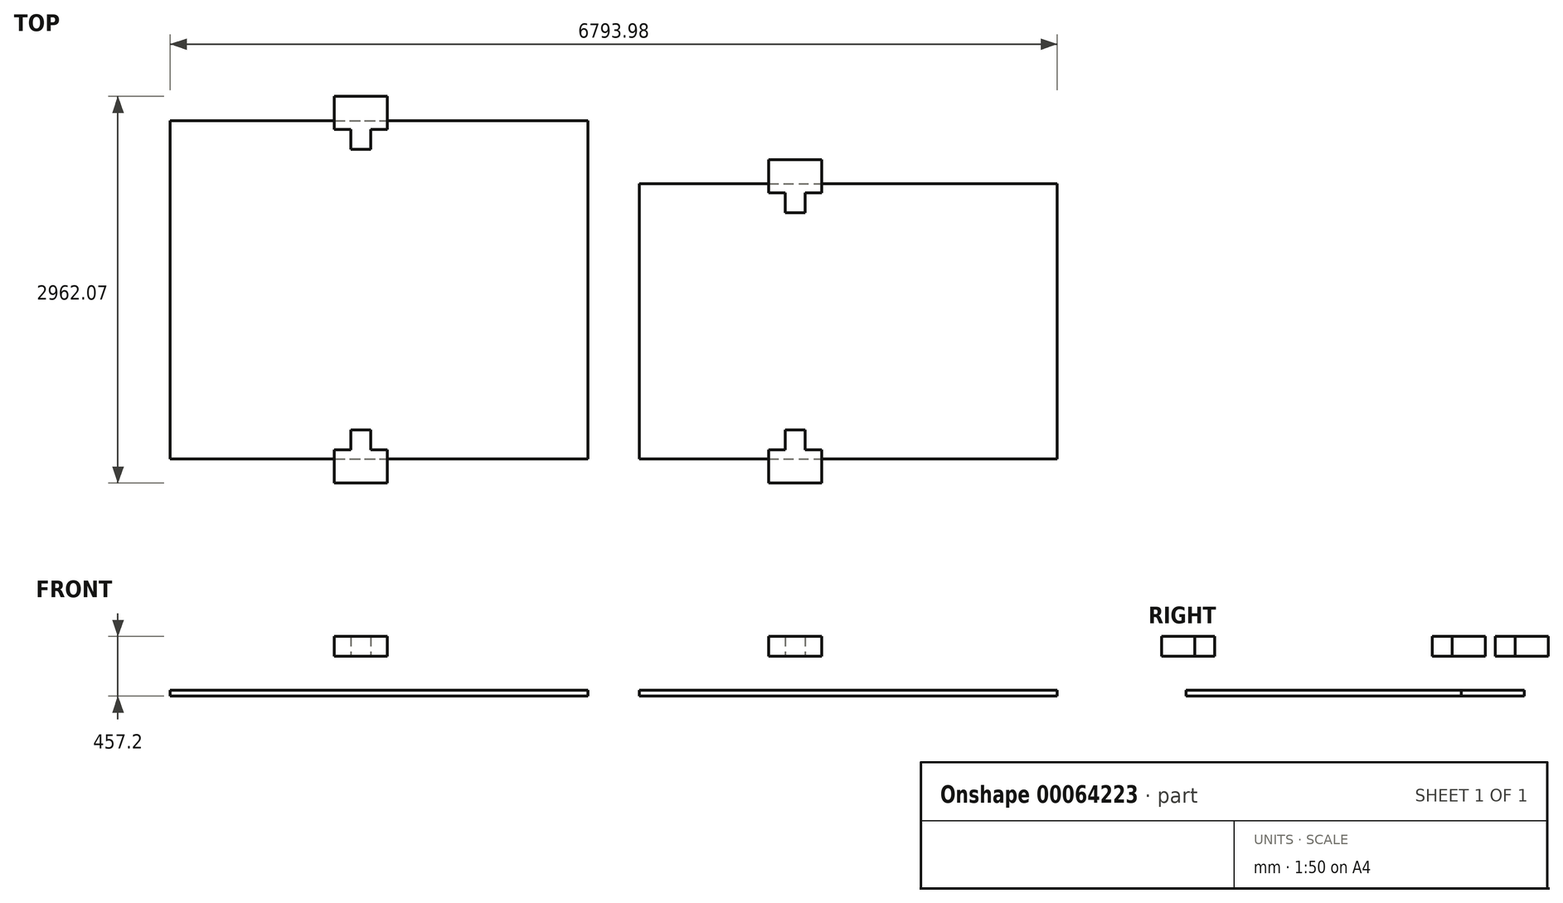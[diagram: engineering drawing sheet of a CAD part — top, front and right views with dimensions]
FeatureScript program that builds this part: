
annotation { "Feature Type Name" : "Feature", "Feature Type Description" : "" }
export const myFeature = defineFeature(function(context is Context, id is Id, definition is map)
    precondition{}
    {
        {
            var Q0;
            Q0=qCreatedBy(makeId("Top.planeOp"),FACE);
            var sketch = newSketch(context, id + "F0", { "sketchPlane" : qUnion([Q0])});
            skLineSegment(sketch, "E0.bottom", {"start": v(-1939.52, -1293.43) * mm, "end": v(1260.88, -1293.43) * mm});
            skLineSegment(sketch, "E0.top", {"start": v(-1939.52, 1297.37) * mm, "end": v(1260.88, 1297.37) * mm});
            skLineSegment(sketch, "E0.left", {"start": v(-1939.52, -1293.43) * mm, "end": v(-1939.52, 1297.37) * mm});
            skLineSegment(sketch, "E0.right", {"start": v(1260.88, -1293.43) * mm, "end": v(1260.88, 1297.37) * mm});
            skSolve(sketch);
        }
        {
            var Q0;
            Q0=makeQuery(id+"F0.imprint","IMPRINT",FACE,{"disambiguationData":[TD([[makeQuery(id+"F0.imprint","IMPRINT",EDGE,{"derivedFrom":sQuery(id+"F0.wireOp",EDGE,"E0.bottom")}),1.0]])]});
            extrude(context, id + "F1", {"entities" : qUnion([Q0]), "depth" : 44.45 * mm});
        }
        {
            var Q0;
            Q0=qCreatedBy(makeId("Top.planeOp"),FACE);
            var sketch = newSketch(context, id + "F2", { "sketchPlane" : qUnion([Q0])});
            skLineSegment(sketch, "E1.bottom", {"start": v(1654.06, 814.34) * mm, "end": v(4854.46, 814.34) * mm});
            skLineSegment(sketch, "E1.top", {"start": v(1654.06, -1293.86) * mm, "end": v(4854.46, -1293.86) * mm});
            skLineSegment(sketch, "E1.left", {"start": v(1654.06, 814.34) * mm, "end": v(1654.06, -1293.86) * mm});
            skLineSegment(sketch, "E1.right", {"start": v(4854.46, 814.34) * mm, "end": v(4854.46, -1293.86) * mm});
            skSolve(sketch);
        }
        {
            var Q0;
            Q0=makeQuery(id+"F2.imprint","IMPRINT",FACE,{"disambiguationData":[TD([[makeQuery(id+"F2.imprint","IMPRINT",EDGE,{"derivedFrom":sQuery(id+"F2.wireOp",EDGE,"E1.bottom")}),-1.0]])]});
            extrude(context, id + "F3", {"entities" : qUnion([Q0]), "depth" : 44.45 * mm});
        }
        {
            var Q0;
            Q0=makeQuery(id+"F1.opExtrude","CAP_FACE",FACE,{"disambiguationData":[OSD([sQuery(id+"F0.wireOp",EDGE,"E0.bottom"),sQuery(id+"F0.wireOp",EDGE,"E0.top"),sQuery(id+"F0.wireOp",EDGE,"E0.left"),sQuery(id+"F0.wireOp",EDGE,"E0.right")])],"isStart":false});
            var sketch = newSketch(context, id + "F4", { "sketchPlane" : qUnion([Q0])});
            skLineSegment(sketch, "E2.0", {"start": v(-1718.54, 1076.4) * mm, "end": v(1039.9, 1076.4) * mm});
            skLineSegment(sketch, "E2.1", {"start": v(-1718.54, -1072.45) * mm, "end": v(-1718.54, 1076.4) * mm});
            skLineSegment(sketch, "E2.2", {"start": v(-1718.54, -1072.45) * mm, "end": v(1039.9, -1072.45) * mm});
            skLineSegment(sketch, "E2.3", {"start": v(1039.9, -1072.45) * mm, "end": v(1039.9, 1076.4) * mm});
            skSolve(sketch);
        }
        {
            var Q0;
            Q0=makeQuery(id+"F3.opExtrude","CAP_FACE",FACE,{"disambiguationData":[OSD([sQuery(id+"F2.wireOp",EDGE,"E1.bottom"),sQuery(id+"F2.wireOp",EDGE,"E1.top"),sQuery(id+"F2.wireOp",EDGE,"E1.left"),sQuery(id+"F2.wireOp",EDGE,"E1.right")])],"isStart":false});
            var sketch = newSketch(context, id + "F5", { "sketchPlane" : qUnion([Q0])});
            skLineSegment(sketch, "E3.0", {"start": v(1875.04, 593.36) * mm, "end": v(4633.48, 593.36) * mm});
            skLineSegment(sketch, "E3.1", {"start": v(1875.04, 593.36) * mm, "end": v(1875.04, -1072.88) * mm});
            skLineSegment(sketch, "E3.2", {"start": v(1875.04, -1072.88) * mm, "end": v(4633.48, -1072.88) * mm});
            skLineSegment(sketch, "E3.3", {"start": v(4633.48, 593.36) * mm, "end": v(4633.48, -1072.88) * mm});
            skSolve(sketch);
        }
        {
            var Q0;
            Q0=qCreatedBy(makeId("Top.planeOp"),FACE);
            cPlane(context, id + "F6", {"entities" : qUnion([Q0]), "cplaneType" : CPlaneType.OFFSET, "offset" : 304.8 * mm, "width" : 152.4 * mm, "height" : 152.4 * mm});
        }
        {
            var Q0;
            Q0=qCreatedBy(id+"F6.planeOp",FACE);
            var sketch = newSketch(context, id + "F7", { "sketchPlane" : qUnion([Q0])});
            skLineSegment(sketch, "E4.bottom", {"start": v(-682.1, 1482.8) * mm, "end": v(-275.7, 1482.8) * mm});
            skLineSegment(sketch, "E4.top", {"start": v(-682.1, 1228.8) * mm, "end": v(-275.7, 1228.8) * mm});
            skLineSegment(sketch, "E4.left", {"start": v(-682.1, 1482.8) * mm, "end": v(-682.1, 1228.8) * mm});
            skLineSegment(sketch, "E4.right", {"start": v(-275.7, 1482.8) * mm, "end": v(-275.7, 1228.8) * mm});
            skLineSegment(sketch, "E5.bottom", {"start": v(-555.1, 1228.8) * mm, "end": v(-402.7, 1228.8) * mm});
            skLineSegment(sketch, "E5.top", {"start": v(-555.1, 1076.4) * mm, "end": v(-402.7, 1076.4) * mm});
            skLineSegment(sketch, "E5.left", {"start": v(-555.1, 1228.8) * mm, "end": v(-555.1, 1076.4) * mm});
            skLineSegment(sketch, "E5.right", {"start": v(-402.7, 1228.8) * mm, "end": v(-402.7, 1076.4) * mm});
            skLineSegment(sketch, "E6", {"start": v(-1718.54, 1.97) * mm, "end": v(1039.9, 1.97) * mm});
            skLineSegment(sketch, "E7.MirrorCS", {"start": v(-682.1, -1224.85) * mm, "end": v(-275.7, -1224.85) * mm});
            skLineSegment(sketch, "E8.MirrorCS", {"start": v(-682.1, -1478.85) * mm, "end": v(-275.7, -1478.85) * mm});
            skLineSegment(sketch, "E9.MirrorCS", {"start": v(-275.7, -1478.85) * mm, "end": v(-275.7, -1224.85) * mm});
            skLineSegment(sketch, "E10.MirrorCS", {"start": v(-555.1, -1224.85) * mm, "end": v(-555.1, -1072.45) * mm});
            skLineSegment(sketch, "E11.MirrorCS", {"start": v(-402.7, -1224.85) * mm, "end": v(-402.7, -1072.45) * mm});
            skLineSegment(sketch, "E12.MirrorCS", {"start": v(-555.1, -1072.45) * mm, "end": v(-402.7, -1072.45) * mm});
            skLineSegment(sketch, "E13.MirrorCS", {"start": v(-555.1, -1224.85) * mm, "end": v(-402.7, -1224.85) * mm});
            skLineSegment(sketch, "E14.MirrorCS", {"start": v(-682.1, -1478.85) * mm, "end": v(-682.1, -1224.85) * mm});
            skSolve(sketch);
        }
        {
            var Q0;
            Q0 = qSketchRegion(id + "F7", true);
            extrude(context, id + "F8", {"entities" : qUnion([Q0]), "depth" : 152.4 * mm});
        }
        {
            var Q0;
            Q0=qCreatedBy(id+"F6.planeOp",FACE);
            var sketch = newSketch(context, id + "F9", { "sketchPlane" : qUnion([Q0])});
            skLineSegment(sketch, "E15.bottom", {"start": v(2771.38, 745.76) * mm, "end": v(2923.78, 745.76) * mm});
            skLineSegment(sketch, "E15.top", {"start": v(2771.38, 593.36) * mm, "end": v(2923.78, 593.36) * mm});
            skLineSegment(sketch, "E15.left", {"start": v(2771.38, 745.76) * mm, "end": v(2771.38, 593.36) * mm});
            skLineSegment(sketch, "E15.right", {"start": v(2923.78, 745.76) * mm, "end": v(2923.78, 593.36) * mm});
            skLineSegment(sketch, "E16.bottom", {"start": v(2644.38, 999.76) * mm, "end": v(3050.78, 999.76) * mm});
            skLineSegment(sketch, "E16.top", {"start": v(2644.38, 745.76) * mm, "end": v(3050.78, 745.76) * mm});
            skLineSegment(sketch, "E16.left", {"start": v(2644.38, 999.76) * mm, "end": v(2644.38, 745.76) * mm});
            skLineSegment(sketch, "E16.right", {"start": v(3050.78, 999.76) * mm, "end": v(3050.78, 745.76) * mm});
            skLineSegment(sketch, "E17", {"start": v(1875.04, -239.76) * mm, "end": v(4633.48, -239.76) * mm});
            skLineSegment(sketch, "E18.MirrorCS", {"start": v(2771.38, -1225.28) * mm, "end": v(2923.78, -1225.28) * mm});
            skLineSegment(sketch, "E19.MirrorCS", {"start": v(2923.78, -1225.28) * mm, "end": v(2923.78, -1072.88) * mm});
            skLineSegment(sketch, "E20.MirrorCS", {"start": v(2644.38, -1479.28) * mm, "end": v(3050.78, -1479.28) * mm});
            skLineSegment(sketch, "E21.MirrorCS", {"start": v(2644.38, -1225.28) * mm, "end": v(3050.78, -1225.28) * mm});
            skLineSegment(sketch, "E22.MirrorCS", {"start": v(2771.38, -1072.88) * mm, "end": v(2923.78, -1072.88) * mm});
            skLineSegment(sketch, "E23.MirrorCS", {"start": v(2644.38, -1479.28) * mm, "end": v(2644.38, -1225.28) * mm});
            skLineSegment(sketch, "E24.MirrorCS", {"start": v(2771.38, -1225.28) * mm, "end": v(2771.38, -1072.88) * mm});
            skLineSegment(sketch, "E25.MirrorCS", {"start": v(3050.78, -1479.28) * mm, "end": v(3050.78, -1225.28) * mm});
            skSolve(sketch);
        }
        {
            var Q0;
            Q0 = qSketchRegion(id + "F9", true);
            extrude(context, id + "F10", {"entities" : qUnion([Q0]), "depth" : 152.4 * mm});
        }
    });
